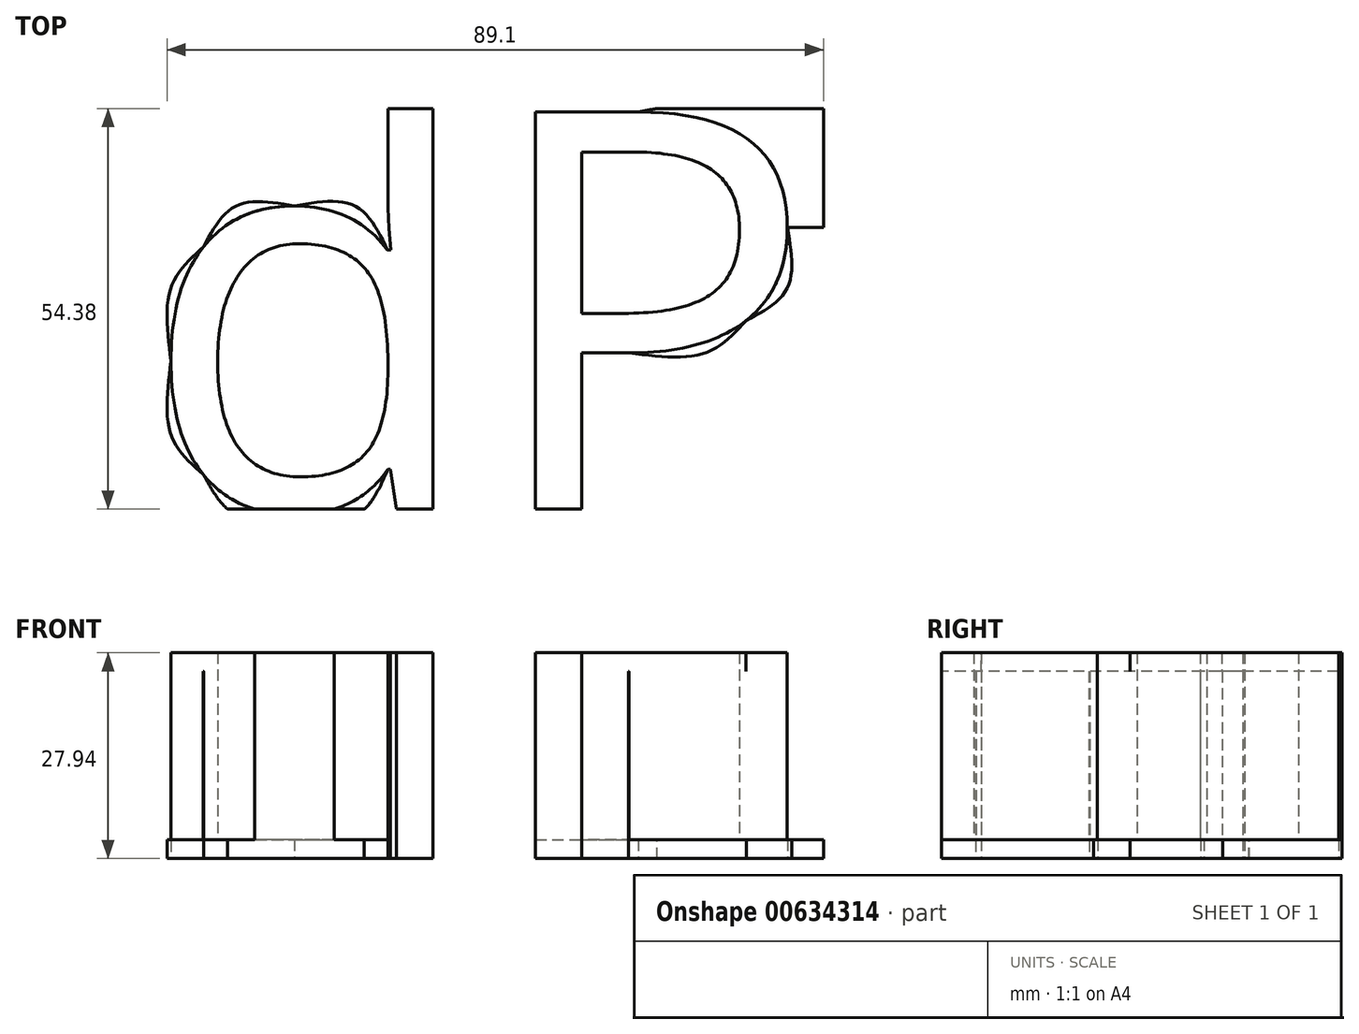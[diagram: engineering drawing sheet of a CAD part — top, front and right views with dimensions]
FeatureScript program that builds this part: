
annotation { "Feature Type Name" : "Feature", "Feature Type Description" : "" }
export const myFeature = defineFeature(function(context is Context, id is Id, definition is map)
    precondition{}
    {
        {
            var Q0;
            Q0=qCreatedBy(makeId("Top.planeOp"),FACE);
            var sketch = newSketch(context, id + "F0", { "sketchPlane" : qUnion([Q0])});
            skLineSegment(sketch, "E0", {"start": v(0, 0) * mm, "end": v(0, -27.2) * mm});
            skLineSegment(sketch, "E1", {"start": v(0, -27.2) * mm, "end": v(-46.4, -27.2) * mm});
            skLineSegment(sketch, "E2", {"start": v(-46.4, -27.2) * mm, "end": v(-46.4, 0) * mm});
            skPoint(sketch, "E3.start.orphan", {"position": v(0, 26.27) * mm});
            skLineSegment(sketch, "E4", {"start": v(-46.4, 0) * mm, "end": v(0, 0) * mm});
            skLineSegment(sketch, "E5.MirrorCS", {"start": v(0, 27.2) * mm, "end": v(-46.4, 27.2) * mm});
            skLineSegment(sketch, "E6.MirrorCS", {"start": v(-46.4, 27.2) * mm, "end": v(-46.4, 0) * mm});
            skLineSegment(sketch, "E7.MirrorCS", {"start": v(0, 0) * mm, "end": v(0, 27.2) * mm});
            skLineSegment(sketch, "E8.MirrorCS", {"start": v(46.4, 0) * mm, "end": v(0, 0) * mm});
            skLineSegment(sketch, "E9.MirrorCS", {"start": v(0, -27.2) * mm, "end": v(46.4, -27.2) * mm});
            skLineSegment(sketch, "E10.MirrorCS", {"start": v(46.4, -27.2) * mm, "end": v(46.4, 0) * mm});
            skLineSegment(sketch, "E11.MirrorCS", {"start": v(46.4, 27.2) * mm, "end": v(46.4, 0) * mm});
            skLineSegment(sketch, "E12.MirrorCS", {"start": v(0, 27.2) * mm, "end": v(46.4, 27.2) * mm});
            skSolve(sketch);
        }
        {
            var Q0;
            Q0 = qSketchRegion(id + "F0", true);
            extrude(context, id + "F1", {"entities" : qUnion([Q0]), "depth" : 2.54 * mm, "offsetDistance" : 25.4 * mm});
        }
        {
            var Q0;
            Q0=makeQuery(id+"F1.opExtrude","CAP_FACE",FACE,{"disambiguationData":[OSD([sQuery(id+"F0.wireOp",EDGE,"E1"),sQuery(id+"F0.wireOp",EDGE,"E2"),sQuery(id+"F0.wireOp",EDGE,"E5.MirrorCS"),sQuery(id+"F0.wireOp",EDGE,"E6.MirrorCS"),sQuery(id+"F0.wireOp",EDGE,"E9.MirrorCS"),sQuery(id+"F0.wireOp",EDGE,"E10.MirrorCS"),sQuery(id+"F0.wireOp",EDGE,"E11.MirrorCS"),sQuery(id+"F0.wireOp",EDGE,"E12.MirrorCS")])],"isStart":false});
            var sketch = newSketch(context, id + "F2", { "sketchPlane" : qUnion([Q0])});
            skLineSegment(sketch, "E13.0.0", {"start": v(46.4, 27.2) * mm, "end": v(-46.4, 27.2) * mm});
            skLineSegment(sketch, "E13.0.1", {"start": v(-46.4, 27.2) * mm, "end": v(-46.4, -27.2) * mm});
            skLineSegment(sketch, "E13.0.2", {"start": v(-46.4, -27.2) * mm, "end": v(46.4, -27.2) * mm});
            skLineSegment(sketch, "E13.0.3", {"start": v(46.4, -27.2) * mm, "end": v(46.4, 27.2) * mm});
            skText(sketch, "E14", { "text": "dP\n", "fontName": "OpenSans-Regular.ttf"});
            const initialGuessF2  = {"E14": [-0.0464, -0.0272, 1, 0, 0.05438]};
            skSetInitialGuess(sketch, initialGuessF2);
            skSolve(sketch);
        }
        {
            var Q0;
            {var subQ8=sQuery(id+"F2.wireOp",EDGE,"E14.sketch_text.stroke-0");Q0=makeQuery(id+"F2.imprint","IMPRINT",FACE,{"disambiguationData":[TD([[makeQuery(id+"F2.imprint","IMPRINT",EDGE,{"derivedFrom":subQ8}),-1.0]])]});}
            var Q1;
            Q1=makeQuery(id+"F2.imprint","IMPRINT",FACE,{"disambiguationData":[TD([[makeQuery(id+"F2.imprint","IMPRINT",EDGE,{"derivedFrom":sQuery(id+"F2.wireOp",EDGE,"E14.sketch_text.stroke-24")}),-1.0]])]});
            extrude(context, id + "F3", {"entities" : qUnion([Q0, Q1]), "operationType" : NewBodyOperationType.ADD, "depth" : 25.4 * mm, "offsetDistance" : 25.4 * mm});
        }
        {
            var Q0;
            Q0=makeQuery(id+"F1.opExtrude","CAP_FACE",FACE,{"disambiguationData":[OSD([sQuery(id+"F0.wireOp",EDGE,"E1"),sQuery(id+"F0.wireOp",EDGE,"E2"),sQuery(id+"F0.wireOp",EDGE,"E5.MirrorCS"),sQuery(id+"F0.wireOp",EDGE,"E6.MirrorCS"),sQuery(id+"F0.wireOp",EDGE,"E9.MirrorCS"),sQuery(id+"F0.wireOp",EDGE,"E10.MirrorCS"),sQuery(id+"F0.wireOp",EDGE,"E11.MirrorCS"),sQuery(id+"F0.wireOp",EDGE,"E12.MirrorCS")])],"isStart":true});
            var sketch = newSketch(context, id + "F4", { "sketchPlane" : qUnion([Q0])});
            skLineSegment(sketch, "E15.0.0", {"start": v(-46.4, -27.2) * mm, "end": v(46.4, -27.2) * mm});
            skLineSegment(sketch, "E15.0.1", {"start": v(46.4, -27.2) * mm, "end": v(46.4, 27.2) * mm});
            skLineSegment(sketch, "E15.0.2", {"start": v(46.4, 27.2) * mm, "end": v(-46.4, 27.2) * mm});
            skLineSegment(sketch, "E15.0.3", {"start": v(-46.4, 27.2) * mm, "end": v(-46.4, -27.2) * mm});
            skLineSegment(sketch, "E16.0.0", {"start": v(-6.6, 27.2) * mm, "end": v(-6.6, -27.2) * mm});
            skLineSegment(sketch, "E16.0.1", {"start": v(-6.6, -27.2) * mm, "end": v(-12.72, -27.2) * mm});
            skLineSegment(sketch, "E16.0.2", {"start": v(-12.72, -27.2) * mm, "end": v(-12.72, -13.75) * mm});
            skLineSegment(sketch, "E16.0.3", {"start": v(-12.72, -13.75) * mm, "end": v(-12.57, -10.9) * mm});
            skLineSegment(sketch, "E16.0.4", {"start": v(-12.57, -10.9) * mm, "end": v(-12.3, -8) * mm});
            skLineSegment(sketch, "E16.0.5", {"start": v(-12.3, -8) * mm, "end": v(-12.8, -8) * mm});
            skFitSpline(sketch, "E16.0.6", {"points": [v(-12.8, -8) * mm, v(-17.18, -13.97) * mm, v(-25.41, -13.97) * mm]});
            skFitSpline(sketch, "E16.0.7", {"points": [v(-25.41, -13.97) * mm, v(-33.3, -13.97) * mm, v(-37.73, -8.44) * mm]});
            skFitSpline(sketch, "E16.0.8", {"points": [v(-37.73, -8.44) * mm, v(-42.16, -2.9) * mm, v(-42.16, 7.1) * mm]});
            skFitSpline(sketch, "E16.0.9", {"points": [v(-42.16, 7.1) * mm, v(-42.16, 17.09) * mm, v(-37.75, 22.51) * mm]});
            skFitSpline(sketch, "E16.0.10", {"points": [v(-37.75, 22.51) * mm, v(-33.34, 27.94) * mm, v(-25.41, 27.94) * mm]});
            skLineSegment(sketch, "E16.0.11", {"start": v(-30.8, 27.2) * mm, "end": v(-20.05, 27.2) * mm});
            skFitSpline(sketch, "E16.0.12", {"points": [v(-25.41, 27.94) * mm, v(-16.96, 27.94) * mm, v(-12.72, 21.78) * mm]});
            skLineSegment(sketch, "E16.0.13", {"start": v(-12.72, 21.78) * mm, "end": v(-12.4, 21.78) * mm});
            skLineSegment(sketch, "E16.0.14", {"start": v(-12.4, 21.78) * mm, "end": v(-11.58, 27.2) * mm});
            skLineSegment(sketch, "E16.0.15", {"start": v(-11.58, 27.2) * mm, "end": v(-6.6, 27.2) * mm});
            skLineSegment(sketch, "E17.0.0", {"start": v(7.3, -26.73) * mm, "end": v(7.3, 27.2) * mm});
            skLineSegment(sketch, "E17.0.1", {"start": v(7.3, 27.2) * mm, "end": v(13.57, 27.2) * mm});
            skLineSegment(sketch, "E17.0.2", {"start": v(13.57, 27.2) * mm, "end": v(13.57, 5.98) * mm});
            skLineSegment(sketch, "E17.0.3", {"start": v(13.57, 5.98) * mm, "end": v(19.92, 5.98) * mm});
            skFitSpline(sketch, "E17.0.4", {"points": [v(19.92, 5.98) * mm, v(30.32, 5.98) * mm, v(35.9, 1.58) * mm]});
            skFitSpline(sketch, "E17.0.5", {"points": [v(35.9, 1.58) * mm, v(41.5, -2.83) * mm, v(41.5, -11.02) * mm]});
            skFitSpline(sketch, "E17.0.6", {"points": [v(41.5, -11.02) * mm, v(41.5, -26.73) * mm, v(21.3, -26.73) * mm]});
            skLineSegment(sketch, "E17.0.7", {"start": v(21.3, -26.73) * mm, "end": v(7.3, -26.73) * mm});
            skLineSegment(sketch, "E18", {"start": v(-42.16, 7.1) * mm, "end": v(-46.4, 7.1) * mm});
            skLineSegment(sketch, "E19", {"start": v(41.5, -11.02) * mm, "end": v(46.4, -11.02) * mm});
            skSolve(sketch);
        }
        {
            var Q0;
            {var subQ0=sQuery(id+"F4.wireOp",EDGE,"E17.0.2");Q0=makeQuery(id+"F4.imprint","IMPRINT",FACE,{"disambiguationData":[TD([[makeQuery(id+"F4.imprint","IMPRINT",EDGE,{"derivedFrom":subQ0}),1.0]])]});}
            var Q1;
            {var subQ4=sQuery(id+"F4.wireOp",EDGE,"E16.0.0");Q1=makeQuery(id+"F4.imprint","IMPRINT",FACE,{"disambiguationData":[TD([[makeQuery(id+"F4.imprint","IMPRINT",EDGE,{"derivedFrom":subQ4}),1.0]])]});}
            var Q2;
            {var subQ0=sQuery(id+"F4.wireOp",EDGE,"E16.0.2");Q2=makeQuery(id+"F4.imprint","IMPRINT",FACE,{"disambiguationData":[TD([[makeQuery(id+"F4.imprint","IMPRINT",EDGE,{"derivedFrom":subQ0}),1.0]])]});}
            var Q3;
            Q3=makeQuery(id+"F4.imprint","IMPRINT",FACE,{"disambiguationData":[TD([[makeQuery(id+"F4.imprint","IMPRINT",EDGE,{"derivedFrom":sQuery(id+"F4.wireOp",EDGE,"E16.0.9")}),1.0]])]});
            var Q4;
            {var subQ0=sQuery(id+"F4.wireOp",EDGE,"E16.0.12");Q4=makeQuery(id+"F4.imprint","IMPRINT",FACE,{"disambiguationData":[TD([[makeQuery(id+"F4.imprint","IMPRINT",EDGE,{"derivedFrom":subQ0}),1.0]])]});}
            extrude(context, id + "F5", {"entities" : qUnion([Q0, Q1, Q2, Q3, Q4]), "operationType" : NewBodyOperationType.REMOVE, "oppositeDirection" : true, "depth" : 25.4 * mm, "offsetDistance" : 25.4 * mm});
        }
    });
